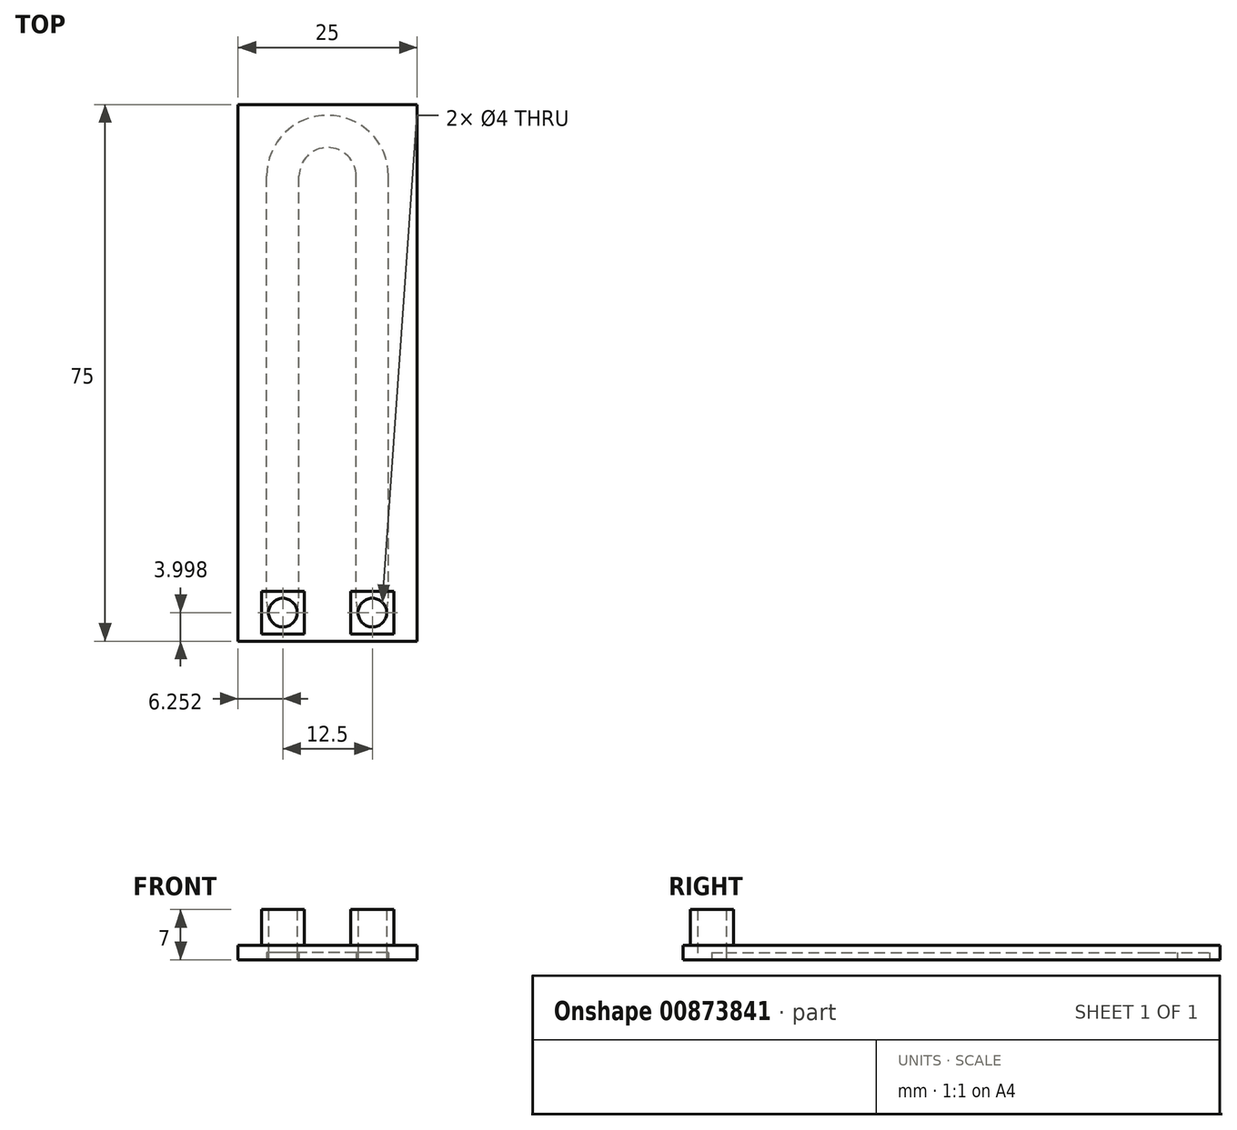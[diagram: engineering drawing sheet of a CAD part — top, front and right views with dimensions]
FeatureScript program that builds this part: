
annotation { "Feature Type Name" : "Feature", "Feature Type Description" : "" }
export const myFeature = defineFeature(function(context is Context, id is Id, definition is map)
    precondition{}
    {
        {
            var Q0;
            Q0=qCreatedBy(makeId("Top.planeOp"),FACE);
            var sketch = newSketch(context, id + "F0", { "sketchPlane" : qUnion([Q0])});
            skLineSegment(sketch, "E0.bottom", {"start": v(-44.29, 25.1) * mm, "end": v(-19.29, 25.1) * mm});
            skLineSegment(sketch, "E0.top", {"start": v(-44.29, -49.9) * mm, "end": v(-19.29, -49.9) * mm});
            skLineSegment(sketch, "E0.left", {"start": v(-44.29, 25.1) * mm, "end": v(-44.29, -49.9) * mm});
            skLineSegment(sketch, "E0.right", {"start": v(-19.29, 25.1) * mm, "end": v(-19.29, -49.9) * mm});
            skPoint(sketch, "E1", {"position": v(-31.79, -49.9) * mm});
            skPoint(sketch, "E2", {"position": v(-19.29, -12.4) * mm});
            skPoint(sketch, "E3", {"position": v(-44.29, -12.4) * mm});
            skPoint(sketch, "E4", {"position": v(-31.79, 25.1) * mm});
            skPoint(sketch, "E5", {"position": v(-31.79, -12.4) * mm});
            skPoint(sketch, "E6", {"position": v(-25.54, -49.9) * mm});
            skPoint(sketch, "E7", {"position": v(-38.04, -49.9) * mm});
            skPoint(sketch, "E8", {"position": v(-25.54, -43.64) * mm});
            skPoint(sketch, "E9", {"position": v(-38.04, -43.64) * mm});
            skSolve(sketch);
        }
        {
            var Q0;
            Q0=makeQuery(id+"F0.imprint","IMPRINT",FACE,{"disambiguationData":[TD([[makeQuery(id+"F0.imprint","IMPRINT",EDGE,{"derivedFrom":sQuery(id+"F0.wireOp",EDGE,"E0.bottom")}),-1.0]])]});
            var sketch = newSketch(context, id + "F1", { "sketchPlane" : qUnion([Q0])});
            skPoint(sketch, "E10", {"position": v(-25.54, -45.9) * mm});
            skPoint(sketch, "E11", {"position": v(-38.04, -45.9) * mm});
            skPoint(sketch, "E12", {"position": v(-31.79, 15.1) * mm});
            skCircle(sketch, "E13", {"center": v(-25.54, -45.9) * mm, "radius": 2 * mm});
            skCircle(sketch, "E14", {"center": v(-38.04, -45.9) * mm, "radius": 2 * mm});
            skPoint(sketch, "E15", {"position": v(-23.54, -45.9) * mm});
            skPoint(sketch, "E16", {"position": v(-27.54, -45.9) * mm});
            skPoint(sketch, "E17", {"position": v(-36.04, -45.9) * mm});
            skPoint(sketch, "E18", {"position": v(-40.04, -45.9) * mm});
            skPoint(sketch, "E19", {"position": v(-38.04, -43.9) * mm});
            skPoint(sketch, "E20", {"position": v(-25.54, -43.9) * mm});
            skPoint(sketch, "E21", {"position": v(-40.29, -43.9) * mm});
            skPoint(sketch, "E22", {"position": v(-35.79, -43.9) * mm});
            skPoint(sketch, "E23", {"position": v(-27.79, -43.9) * mm});
            skPoint(sketch, "E24", {"position": v(-23.29, -43.9) * mm});
            skLineSegment(sketch, "E25", {"start": v(-40.04, -45.9) * mm, "end": v(-40.29, -43.9) * mm});
            skLineSegment(sketch, "E26", {"start": v(-36.04, -45.9) * mm, "end": v(-35.79, -43.9) * mm});
            skLineSegment(sketch, "E27", {"start": v(-27.54, -45.9) * mm, "end": v(-27.79, -43.9) * mm});
            skLineSegment(sketch, "E28", {"start": v(-23.54, -45.9) * mm, "end": v(-23.29, -43.9) * mm});
            skPoint(sketch, "E29", {"position": v(-25.54, 15.1) * mm});
            skPoint(sketch, "E30", {"position": v(-27.79, 15.1) * mm});
            skPoint(sketch, "E31", {"position": v(-23.29, 15.1) * mm});
            skPoint(sketch, "E32", {"position": v(-40.29, 15.1) * mm});
            skPoint(sketch, "E33", {"position": v(-38.04, 15.1) * mm});
            skPoint(sketch, "E34", {"position": v(-35.79, 15.1) * mm});
            skArc(sketch, "E35", {"start": v(-27.79, 15.1) * mm, "mid": v(-31.79, 19.1) * mm, "end": v(-35.79, 15.1) * mm});
            skArc(sketch, "E36", {"start": v(-23.29, 15.1) * mm, "mid": v(-31.79, 23.6) * mm, "end": v(-40.29, 15.1) * mm});
            skLineSegment(sketch, "E37", {"start": v(-40.29, -43.9) * mm, "end": v(-40.29, 15.1) * mm});
            skLineSegment(sketch, "E38", {"start": v(-35.79, -43.9) * mm, "end": v(-35.79, 15.1) * mm});
            skLineSegment(sketch, "E39", {"start": v(-27.79, -43.9) * mm, "end": v(-27.79, 15.1) * mm});
            skLineSegment(sketch, "E40", {"start": v(-23.29, -43.9) * mm, "end": v(-23.29, 15.1) * mm});
            skSolve(sketch);
        }
        {
            var Q0;
            Q0=qCreatedBy(makeId("Top.planeOp"),FACE);
            var sketch = newSketch(context, id + "F2", { "sketchPlane" : qUnion([Q0])});
            skPoint(sketch, "E41", {"position": v(-38.04, -45.9) * mm});
            skPoint(sketch, "E42", {"position": v(-25.54, -45.9) * mm});
            skCircle(sketch, "E43", {"center": v(-38.04, -45.9) * mm, "radius": 2 * mm});
            skCircle(sketch, "E44", {"center": v(-25.54, -45.9) * mm, "radius": 2 * mm});
            skSolve(sketch);
        }
        {
            var Q0;
            Q0=qSketchRegion(id+"F0",true);
            extrude(context, id + "F3", {"entities" : qUnion([Q0]), "depth" : 2 * mm, "offsetDistance" : 25 * mm});
        }
        {
            var Q0;
            Q0=qSketchRegion(id+"F1",true);
            extrude(context, id + "F4", {"entities" : qUnion([Q0]), "operationType" : NewBodyOperationType.REMOVE, "depth" : 1 * mm, "offsetDistance" : 25 * mm});
        }
        {
            var Q0;
            Q0=makeQuery(id+"F3.opExtrude","CAP_FACE",FACE,{"disambiguationData":[OSD([sQuery(id+"F0.wireOp",EDGE,"E0.bottom"),sQuery(id+"F0.wireOp",EDGE,"E0.top"),sQuery(id+"F0.wireOp",EDGE,"E0.left"),sQuery(id+"F0.wireOp",EDGE,"E0.right")])],"isStart":false});
            var sketch = newSketch(context, id + "F5", { "sketchPlane" : qUnion([Q0])});
            skPoint(sketch, "E45", {"position": v(-38.04, -45.9) * mm});
            skPoint(sketch, "E46", {"position": v(-25.54, -45.9) * mm});
            skSolve(sketch);
        }
        {
            var Q0;
            Q0=makeQuery(id+"F5.imprint","IMPRINT",FACE,{"disambiguationData":[TD([[makeQuery(id+"F5.imprint","IMPRINT",EDGE,{"derivedFrom":makeQuery(id+"F3.opExtrude","CAP_EDGE",EDGE,{"disambiguationData":[OSD([sQuery(id+"F0.wireOp",EDGE,"E0.bottom")])],"isStart":false})}),-1.0]])]});
            var sketch = newSketch(context, id + "F6", { "sketchPlane" : qUnion([Q0])});
            skPoint(sketch, "E47", {"position": v(-38.04, -45.9) * mm});
            skPoint(sketch, "E48", {"position": v(-25.54, -45.9) * mm});
            skCircle(sketch, "E49", {"center": v(-38.04, -45.9) * mm, "radius": 2 * mm});
            skCircle(sketch, "E50", {"center": v(-25.54, -45.9) * mm, "radius": 2 * mm});
            skPoint(sketch, "E51", {"position": v(-38.04, -42.9) * mm});
            skPoint(sketch, "E52", {"position": v(-41.04, -42.9) * mm});
            skLineSegment(sketch, "E53.bottom", {"start": v(-41.04, -42.9) * mm, "end": v(-35.04, -42.9) * mm});
            skLineSegment(sketch, "E53.top", {"start": v(-41.04, -48.9) * mm, "end": v(-35.04, -48.9) * mm});
            skLineSegment(sketch, "E53.left", {"start": v(-41.04, -42.9) * mm, "end": v(-41.04, -48.9) * mm});
            skLineSegment(sketch, "E53.right", {"start": v(-35.04, -42.9) * mm, "end": v(-35.04, -48.9) * mm});
            skPoint(sketch, "E54", {"position": v(-25.54, -42.9) * mm});
            skPoint(sketch, "E55", {"position": v(-28.54, -42.9) * mm});
            skLineSegment(sketch, "E56.bottom", {"start": v(-28.54, -42.9) * mm, "end": v(-22.54, -42.9) * mm});
            skLineSegment(sketch, "E56.top", {"start": v(-28.54, -48.9) * mm, "end": v(-22.54, -48.9) * mm});
            skLineSegment(sketch, "E56.left", {"start": v(-28.54, -42.9) * mm, "end": v(-28.54, -48.9) * mm});
            skLineSegment(sketch, "E56.right", {"start": v(-22.54, -42.9) * mm, "end": v(-22.54, -48.9) * mm});
            skSolve(sketch);
        }
        {
            var Q0;
            {var subQ0=sQuery(id+"F1.wireOp",EDGE,"E14");var subQ1=makeQuery(id+"F1.imprint","INTERSECT",VERTEX,{"derivedFrom":[subQ0,sQuery(id+"F1.wireOp",EDGE,"E25")]});Q0=makeQuery(id+"F1.imprint","IMPRINT",FACE,{"disambiguationData":[TD([[makeQuery(id+"F1.imprint","IMPRINT",EDGE,{"disambiguationData":[TD([[subQ1,1.0]])],"derivedFrom":subQ0}),1.0]])]});}
            var Q1;
            {var subQ0=sQuery(id+"F1.wireOp",EDGE,"E13");var subQ1=makeQuery(id+"F1.imprint","INTERSECT",VERTEX,{"derivedFrom":[subQ0,sQuery(id+"F1.wireOp",EDGE,"E27")]});Q1=makeQuery(id+"F1.imprint","IMPRINT",FACE,{"disambiguationData":[TD([[makeQuery(id+"F1.imprint","IMPRINT",EDGE,{"disambiguationData":[TD([[subQ1,1.0]])],"derivedFrom":subQ0}),1.0]])]});}
            extrude(context, id + "F7", {"entities" : qUnion([Q0, Q1]), "operationType" : NewBodyOperationType.REMOVE, "depth" : 7 * mm, "offsetDistance" : 25 * mm});
        }
        {
            var Q0;
            Q0=makeQuery(id+"F6.imprint","IMPRINT",FACE,{"disambiguationData":[TD([[makeQuery(id+"F6.imprint","IMPRINT",EDGE,{"derivedFrom":sQuery(id+"F6.wireOp",EDGE,"E49")}),-1.0]])]});
            var Q1;
            Q1=makeQuery(id+"F6.imprint","IMPRINT",FACE,{"disambiguationData":[TD([[makeQuery(id+"F6.imprint","IMPRINT",EDGE,{"derivedFrom":sQuery(id+"F6.wireOp",EDGE,"E50")}),-1.0]])]});
            extrude(context, id + "F8", {"entities" : qUnion([Q0, Q1]), "operationType" : NewBodyOperationType.ADD, "depth" : 5 * mm, "offsetDistance" : 25 * mm});
        }
    });
